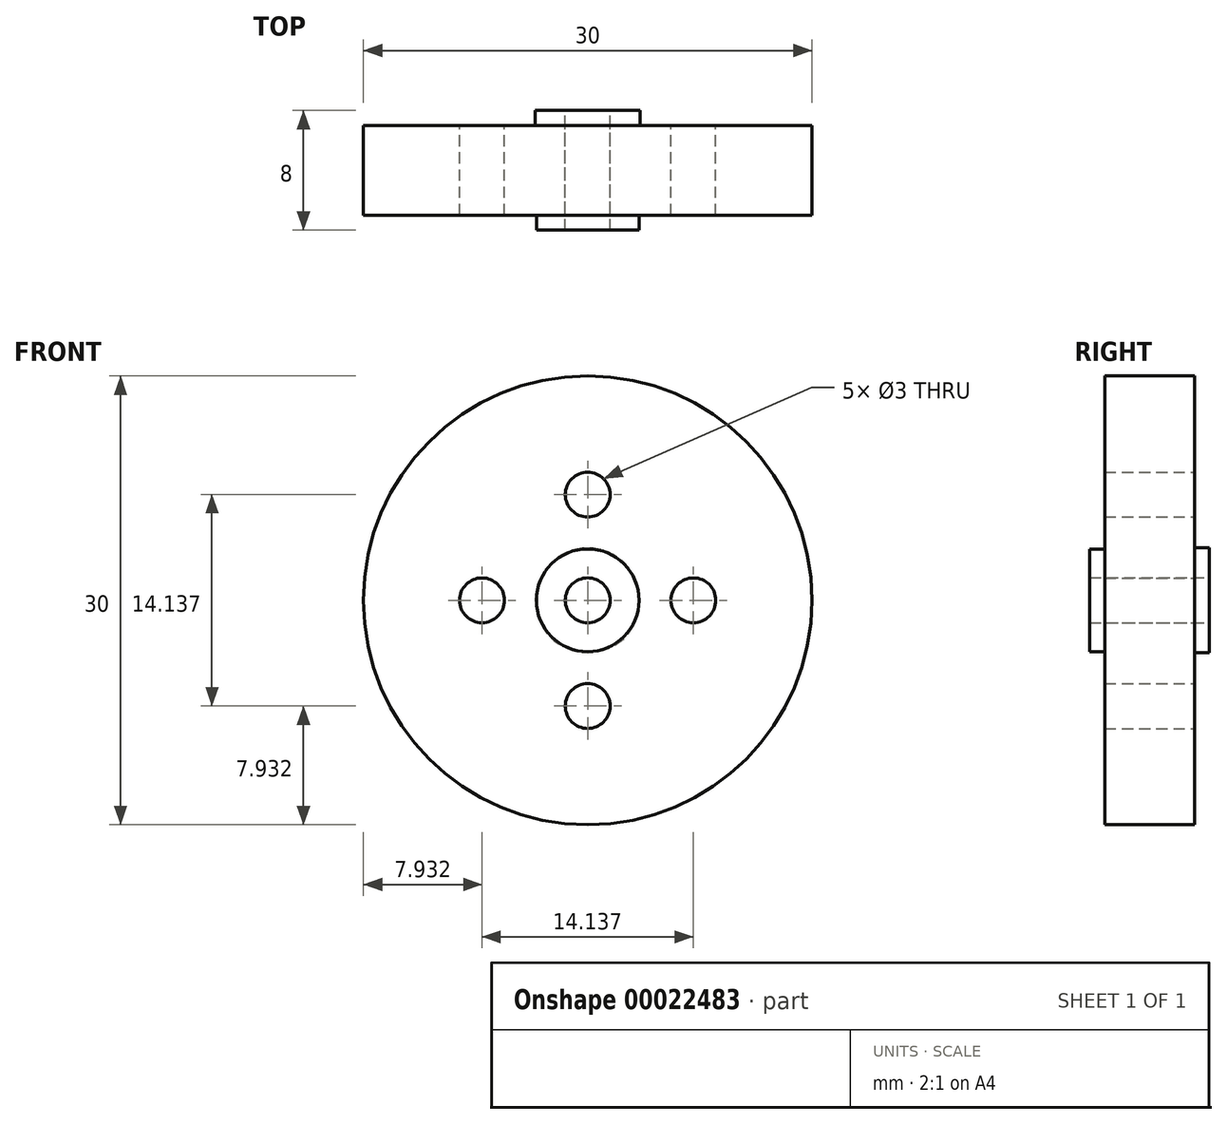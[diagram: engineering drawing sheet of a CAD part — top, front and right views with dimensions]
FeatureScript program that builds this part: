
annotation { "Feature Type Name" : "Feature", "Feature Type Description" : "" }
export const myFeature = defineFeature(function(context is Context, id is Id, definition is map)
    precondition{}
    {
        {
            var Q0;
            Q0=qCreatedBy(makeId("Front.planeOp"),FACE);
            var sketch = newSketch(context, id + "F0", { "sketchPlane" : qUnion([Q0])});
            skCircle(sketch, "E0", {"center": v(0, 0) * mm, "radius": 15 * mm});
            skCircle(sketch, "E1", {"center": v(0, 0) * mm, "radius": 1.5 * mm});
            skCircle(sketch, "E2", {"center": v(0, 0) * mm, "radius": 3.5 * mm});
            skCircle(sketch, "E3", {"center": v(0, 7.07) * mm, "radius": 1.5 * mm});
            skCircle(sketch, "E4.1.0", {"center": v(-7.07, 0) * mm, "radius": 1.5 * mm});
            skCircle(sketch, "E4.2.0", {"center": v(0, -7.07) * mm, "radius": 1.5 * mm});
            skCircle(sketch, "E4.3.0", {"center": v(7.07, 0) * mm, "radius": 1.5 * mm});
            skSolve(sketch);
        }
        {
            var Q0;
            Q0=makeQuery(id+"F0.imprint","IMPRINT",FACE,{"disambiguationData":[TD([[makeQuery(id+"F0.imprint","IMPRINT",EDGE,{"derivedFrom":sQuery(id+"F0.wireOp",EDGE,"E0")}),1.0]])]});
            var Q1;
            Q1=makeQuery(id+"F0.imprint","IMPRINT",FACE,{"disambiguationData":[TD([[makeQuery(id+"F0.imprint","IMPRINT",EDGE,{"derivedFrom":sQuery(id+"F0.wireOp",EDGE,"E1")}),-1.0]])]});
            extrude(context, id + "F1", {"entities" : qUnion([Q0, Q1]), "depth" : 6 * mm});
        }
        {
            var Q0;
            Q0=makeQuery(id+"F1.opExtrude","CAP_FACE",FACE,{"disambiguationData":[OSD([sQuery(id+"F0.wireOp",EDGE,"E0"),sQuery(id+"F0.wireOp",EDGE,"E1"),sQuery(id+"F0.wireOp",EDGE,"E3"),sQuery(id+"F0.wireOp",EDGE,"E4.1.0"),sQuery(id+"F0.wireOp",EDGE,"E4.2.0"),sQuery(id+"F0.wireOp",EDGE,"E4.3.0")])],"isStart":false});
            var sketch = newSketch(context, id + "F2", { "sketchPlane" : qUnion([Q0])});
            skCircle(sketch, "E5", {"center": v(0, 0) * mm, "radius": 3.43 * mm});
            skSolve(sketch);
        }
        {
            var Q0;
            Q0=makeQuery(id+"F2.imprint","IMPRINT",FACE,{"disambiguationData":[TD([[makeQuery(id+"F2.imprint","IMPRINT",EDGE,{"derivedFrom":sQuery(id+"F2.wireOp",EDGE,"E5")}),1.0]])]});
            extrude(context, id + "F3", {"entities" : qUnion([Q0]), "operationType" : NewBodyOperationType.ADD, "depth" : 1 * mm});
        }
        {
            var Q0;
            Q0=makeQuery(id+"F0.imprint","IMPRINT",FACE,{"disambiguationData":[TD([[makeQuery(id+"F0.imprint","IMPRINT",EDGE,{"derivedFrom":sQuery(id+"F0.wireOp",EDGE,"E1")}),-1.0]])]});
            extrude(context, id + "F4", {"entities" : qUnion([Q0]), "operationType" : NewBodyOperationType.ADD, "oppositeDirection" : true, "depth" : 1 * mm});
        }
    });
